# Revit family: OP RIVOLI PLUS
name_source: partatom
category: Plumbing Fixtures
units: mm (PartAtom-declared; Revit-internal decimal feet)

## family parameters
Always vertical = Yes
Cut with Voids When Loaded = No
OmniClass Number = 23.45.00.00
OmniClass Title = Sanitary, Laundry, and Cleaning Equipment
Part Type = Normal
Room Calculation Point = No
Round Connector Dimension = Use Diameter
Shared = Yes
Work Plane-Based = Yes

## types (1)
- OP RIVOLI PLUS
    Accessories = Paquete de fijación, sello de cera, reducción para válvula de admisión de Ø15/16-14 NS-1 a ½-14 NPSM
    Características del Producto = Diseño ergonómico de una sola pieza elongado con asiento y tapa de cierre lento.
    Default Elevation = 30.7"
    Description = One Piece RIVOLI PLUS Trampa Oculta, Elongado, Una Descarga 4.8 l, con Asiento
    Manufacturer = Helvex S.A. de C.V.
    Materials = Cerámica porcelanizada de alto brillo, calidad "A", Tipo l
    Model = OP RIVOLI PLUS
    Presión Máxima de Trabajo = 85.3 psi
    Presión Mínima de Trabajo = 3.6 psi
    Type Comments = Taza oara baño OP RIVOLI PLUS
    URL = http://www.helvex.com
    Valves = Val. de admisión y descarga certificadas, val. de admisión silenciosa, válvulas armadas y calibradas, válvulas de descarga con sello hermético

## geometry (parser evidence)
native form markers: Sweep x3
no freeform markers — native parametric forms only
